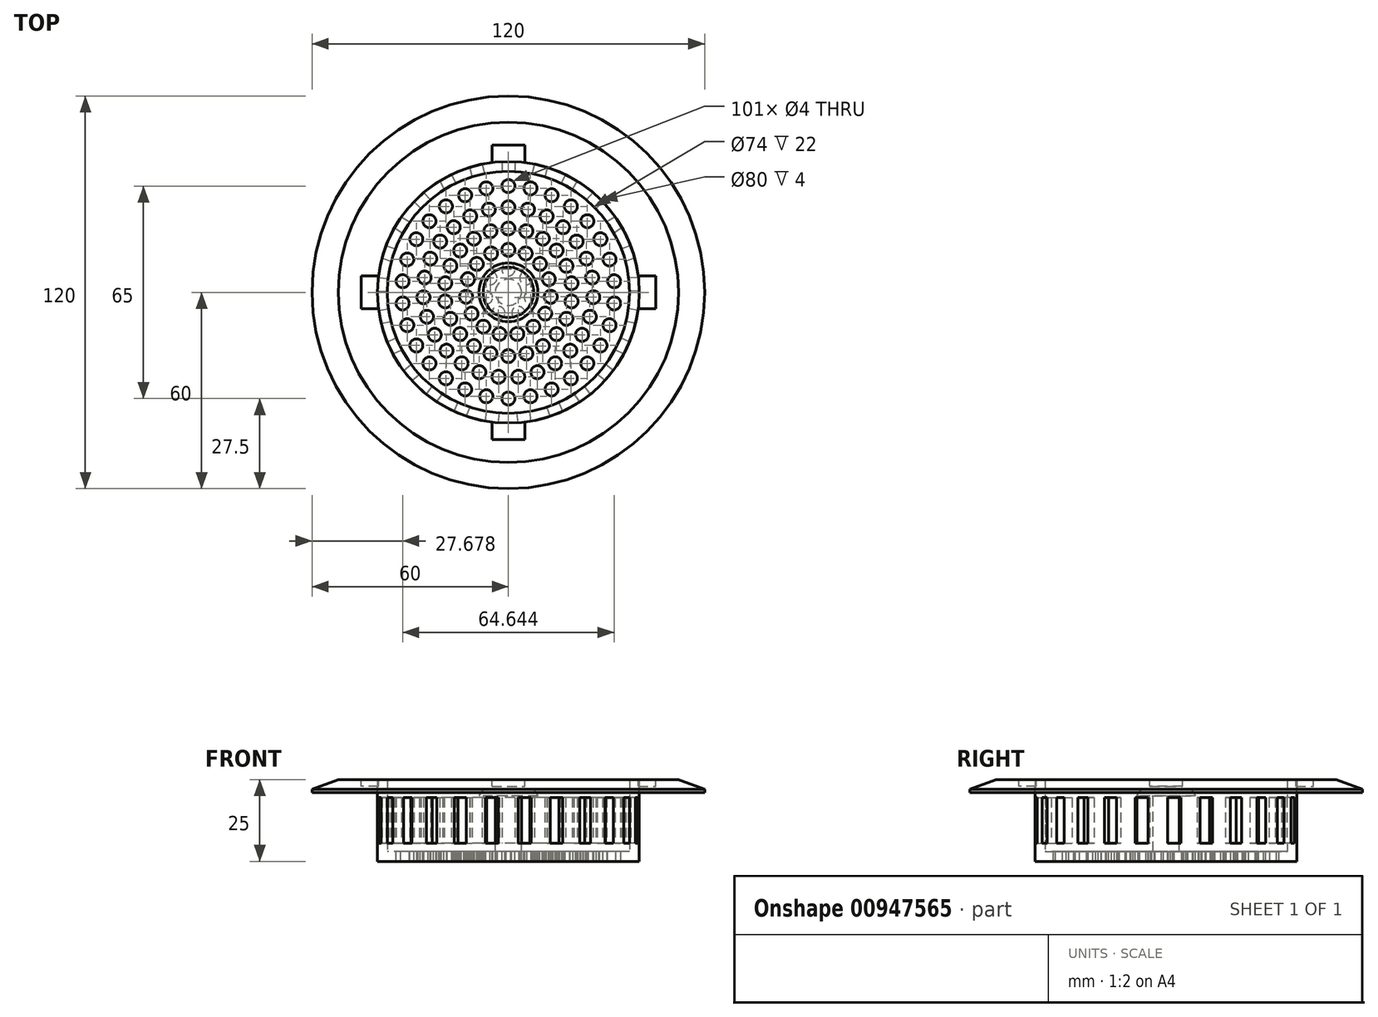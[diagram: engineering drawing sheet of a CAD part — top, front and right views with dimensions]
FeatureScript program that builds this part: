
annotation { "Feature Type Name" : "Feature", "Feature Type Description" : "" }
export const myFeature = defineFeature(function(context is Context, id is Id, definition is map)
    precondition{}
    {
        {
            var Q0;
            Q0=qCreatedBy(makeId("Top.planeOp"),FACE);
            var sketch = newSketch(context, id + "F0", { "sketchPlane" : qUnion([Q0])});
            skCircle(sketch, "E0", {"center": v(0, 0) * mm, "radius": 40 * mm});
            skSolve(sketch);
        }
        {
            var Q0;
            Q0 = qSketchRegion(id + "F0", true);
            extrude(context, id + "F1", {"entities" : qUnion([Q0]), "depth" : 25 * mm, "offsetDistance" : 25 * mm});
        }
        {
            var Q0;
            Q0=makeQuery(id+"F1.opExtrude","CAP_FACE",FACE,{"disambiguationData":[OSD([sQuery(id+"F0.wireOp",EDGE,"E0")])],"isStart":false});
            shell(context, id + "F2", {"entities" : qUnion([Q0]), "thickness" : 3 * mm});
        }
        {
            var Q0;
            Q0=makeQuery(id+"F1.opExtrude","CAP_FACE",FACE,{"disambiguationData":[OSD([sQuery(id+"F0.wireOp",EDGE,"E0")])],"isStart":false});
            var sketch = newSketch(context, id + "F3", { "sketchPlane" : qUnion([Q0])});
            skLineSegment(sketch, "E1", {"start": v(-5, 39.69) * mm, "end": v(-5, 45) * mm});
            skLineSegment(sketch, "E2", {"start": v(-5, 45) * mm, "end": v(0, 45) * mm});
            skLineSegment(sketch, "E3.MirrorCS", {"start": v(5, 45) * mm, "end": v(0, 45) * mm});
            skLineSegment(sketch, "E4.MirrorCS", {"start": v(5, 39.69) * mm, "end": v(5, 45) * mm});
            skLineSegment(sketch, "E5.1.0", {"start": v(-39.69, -5) * mm, "end": v(-45, -5) * mm});
            skLineSegment(sketch, "E5.1.1", {"start": v(-45, -5) * mm, "end": v(-45, 0) * mm});
            skLineSegment(sketch, "E5.1.2", {"start": v(-45, 5) * mm, "end": v(-45, 0) * mm});
            skLineSegment(sketch, "E5.1.3", {"start": v(-39.69, 5) * mm, "end": v(-45, 5) * mm});
            skLineSegment(sketch, "E5.2.0", {"start": v(5, -39.69) * mm, "end": v(5, -45) * mm});
            skLineSegment(sketch, "E5.2.1", {"start": v(5, -45) * mm, "end": v(0, -45) * mm});
            skLineSegment(sketch, "E5.2.2", {"start": v(-5, -45) * mm, "end": v(0, -45) * mm});
            skLineSegment(sketch, "E5.2.3", {"start": v(-5, -39.69) * mm, "end": v(-5, -45) * mm});
            skLineSegment(sketch, "E5.3.0", {"start": v(39.69, 5) * mm, "end": v(45, 5) * mm});
            skLineSegment(sketch, "E5.3.1", {"start": v(45, 5) * mm, "end": v(45, 0) * mm});
            skLineSegment(sketch, "E5.3.2", {"start": v(45, -5) * mm, "end": v(45, 0) * mm});
            skLineSegment(sketch, "E5.3.3", {"start": v(39.69, -5) * mm, "end": v(45, -5) * mm});
            skPoint(sketch, "E5.center", {"position": v(0, 0) * mm});
            skSolve(sketch);
        }
        {
            var Q0;
            {var subQ1=sQuery(id+"F3.wireOp",EDGE,"E5.1.0");Q0=makeQuery(id+"F3.imprint","IMPRINT",FACE,{"disambiguationData":[TD([[makeQuery(id+"F3.imprint","IMPRINT",EDGE,{"derivedFrom":subQ1}),-1.0]])]});}
            var Q1;
            {var subQ1=sQuery(id+"F3.wireOp",EDGE,"E1");Q1=makeQuery(id+"F3.imprint","IMPRINT",FACE,{"disambiguationData":[TD([[makeQuery(id+"F3.imprint","IMPRINT",EDGE,{"derivedFrom":subQ1}),-1.0]])]});}
            var Q2;
            {var subQ1=sQuery(id+"F3.wireOp",EDGE,"E5.3.0");Q2=makeQuery(id+"F3.imprint","IMPRINT",FACE,{"disambiguationData":[TD([[makeQuery(id+"F3.imprint","IMPRINT",EDGE,{"derivedFrom":subQ1}),-1.0]])]});}
            var Q3;
            {var subQ1=sQuery(id+"F3.wireOp",EDGE,"E5.2.0");Q3=makeQuery(id+"F3.imprint","IMPRINT",FACE,{"disambiguationData":[TD([[makeQuery(id+"F3.imprint","IMPRINT",EDGE,{"derivedFrom":subQ1}),-1.0]])]});}
            extrude(context, id + "F4", {"entities" : qUnion([Q0, Q1, Q2, Q3]), "operationType" : NewBodyOperationType.ADD, "oppositeDirection" : true, "depth" : 2 * mm, "offsetDistance" : 25 * mm});
        }
        {
            var Q0;
            {var subQ0=sQuery(id+"F0.wireOp",EDGE,"E0");Q0=makeQuery(id+"F4.boolean.opBoolean","MERGE",FACE,{"derivedFrom":[makeQuery(id+"F1.opExtrude","CAP_FACE",FACE,{"disambiguationData":[OSD([subQ0])],"isStart":false}),makeQuery(id+"F4.opExtrude","CAP_FACE",FACE,{"disambiguationData":[OSD([subQ0,sQuery(id+"F3.wireOp",EDGE,"E1"),sQuery(id+"F3.wireOp",EDGE,"E2"),sQuery(id+"F3.wireOp",EDGE,"E3.MirrorCS"),sQuery(id+"F3.wireOp",EDGE,"E4.MirrorCS")])],"isStart":true}),makeQuery(id+"F4.opExtrude","CAP_FACE",FACE,{"disambiguationData":[OSD([subQ0,sQuery(id+"F3.wireOp",EDGE,"E5.1.0"),sQuery(id+"F3.wireOp",EDGE,"E5.1.1"),sQuery(id+"F3.wireOp",EDGE,"E5.1.2"),sQuery(id+"F3.wireOp",EDGE,"E5.1.3")])],"isStart":true}),makeQuery(id+"F4.opExtrude","CAP_FACE",FACE,{"disambiguationData":[OSD([subQ0,sQuery(id+"F3.wireOp",EDGE,"E5.2.0"),sQuery(id+"F3.wireOp",EDGE,"E5.2.1"),sQuery(id+"F3.wireOp",EDGE,"E5.2.2"),sQuery(id+"F3.wireOp",EDGE,"E5.2.3")])],"isStart":true}),makeQuery(id+"F4.opExtrude","CAP_FACE",FACE,{"disambiguationData":[OSD([subQ0,sQuery(id+"F3.wireOp",EDGE,"E5.3.0"),sQuery(id+"F3.wireOp",EDGE,"E5.3.1"),sQuery(id+"F3.wireOp",EDGE,"E5.3.2"),sQuery(id+"F3.wireOp",EDGE,"E5.3.3")])],"isStart":true})]});}
            var sketch = newSketch(context, id + "F5", { "sketchPlane" : qUnion([Q0])});
            skCircle(sketch, "E6", {"center": v(0, 0) * mm, "radius": 40 * mm});
            skCircle(sketch, "E7.0", {"center": v(0, 0) * mm, "radius": 60 * mm});
            skSolve(sketch);
        }
        {
            var Q0;
            Q0 = qSketchRegion(id + "F5", true);
            extrude(context, id + "F6", {"entities" : qUnion([Q0]), "oppositeDirection" : true, "depth" : 4 * mm, "offsetDistance" : 25 * mm});
        }
        {
            var Q0;
            {var subQ1=sQuery(id+"F3.wireOp",EDGE,"E1");Q0=makeQuery(id+"F3.imprint","IMPRINT",FACE,{"disambiguationData":[TD([[makeQuery(id+"F3.imprint","IMPRINT",EDGE,{"derivedFrom":subQ1}),-1.0]])]});}
            var Q1;
            {var subQ1=sQuery(id+"F3.wireOp",EDGE,"E5.3.0");Q1=makeQuery(id+"F3.imprint","IMPRINT",FACE,{"disambiguationData":[TD([[makeQuery(id+"F3.imprint","IMPRINT",EDGE,{"derivedFrom":subQ1}),-1.0]])]});}
            var Q2;
            {var subQ1=sQuery(id+"F3.wireOp",EDGE,"E5.2.0");Q2=makeQuery(id+"F3.imprint","IMPRINT",FACE,{"disambiguationData":[TD([[makeQuery(id+"F3.imprint","IMPRINT",EDGE,{"derivedFrom":subQ1}),-1.0]])]});}
            var Q3;
            {var subQ1=sQuery(id+"F3.wireOp",EDGE,"E5.1.0");Q3=makeQuery(id+"F3.imprint","IMPRINT",FACE,{"disambiguationData":[TD([[makeQuery(id+"F3.imprint","IMPRINT",EDGE,{"derivedFrom":subQ1}),-1.0]])]});}
            extrude(context, id + "F7", {"entities" : qUnion([Q0, Q1, Q2, Q3]), "operationType" : NewBodyOperationType.REMOVE, "oppositeDirection" : true, "depth" : 2 * mm, "offsetDistance" : 25 * mm});
        }
        {
            var Q0;
            {var subQ0=sQuery(id+"F0.wireOp",EDGE,"E0");Q0=makeQuery(id+"F2.opShell","OFFSET_FACE",FACE,{"disambiguationData":[OSD([subQ0]),TDD([makeQuery(id+"F1.opExtrude","CAP_FACE",FACE,{"disambiguationData":[OSD([subQ0])],"isStart":true})])]});}
            var sketch = newSketch(context, id + "F8", { "sketchPlane" : qUnion([Q0])});
            skLineSegment(sketch, "E8", {"start": v(0, 82.02) * mm, "end": v(0, -74.82) * mm, "construction": true});
            skLineSegment(sketch, "E9", {"start": v(79.98, 0) * mm, "end": v(-98.2, 0) * mm, "construction": true});
            skCircle(sketch, "E10", {"center": v(0, 32.5) * mm, "radius": 2 * mm});
            skCircle(sketch, "E11", {"center": v(0, 26) * mm, "radius": 2 * mm});
            skCircle(sketch, "E12", {"center": v(0, 19.5) * mm, "radius": 2 * mm});
            skCircle(sketch, "E13", {"center": v(0, 13) * mm, "radius": 2 * mm});
            skCircle(sketch, "E14", {"center": v(0, 7) * mm, "radius": 2 * mm});
            skCircle(sketch, "E15.1.0", {"center": v(-6.76, 31.79) * mm, "radius": 2 * mm});
            skCircle(sketch, "E15.2.0", {"center": v(-13.22, 29.7) * mm, "radius": 2 * mm});
            skCircle(sketch, "E15.3.0", {"center": v(-19.1, 26.3) * mm, "radius": 2 * mm});
            skCircle(sketch, "E15.4.0", {"center": v(-24.15, 21.75) * mm, "radius": 2 * mm});
            skCircle(sketch, "E15.5.0", {"center": v(-28.15, 16.25) * mm, "radius": 2 * mm});
            skCircle(sketch, "E15.6.0", {"center": v(-30.9, 10.04) * mm, "radius": 2 * mm});
            skCircle(sketch, "E15.7.0", {"center": v(-32.32, 3.4) * mm, "radius": 2 * mm});
            skCircle(sketch, "E15.8.0", {"center": v(-32.32, -3.4) * mm, "radius": 2 * mm});
            skCircle(sketch, "E15.9.0", {"center": v(-30.9, -10.04) * mm, "radius": 2 * mm});
            skCircle(sketch, "E15.10.0", {"center": v(-28.15, -16.25) * mm, "radius": 2 * mm});
            skCircle(sketch, "E15.11.0", {"center": v(-24.15, -21.75) * mm, "radius": 2 * mm});
            skCircle(sketch, "E15.12.0", {"center": v(-19.1, -26.3) * mm, "radius": 2 * mm});
            skCircle(sketch, "E15.13.0", {"center": v(-13.22, -29.7) * mm, "radius": 2 * mm});
            skCircle(sketch, "E15.14.0", {"center": v(-6.76, -31.79) * mm, "radius": 2 * mm});
            skCircle(sketch, "E15.15.0", {"center": v(0, -32.5) * mm, "radius": 2 * mm});
            skCircle(sketch, "E15.16.0", {"center": v(6.76, -31.79) * mm, "radius": 2 * mm});
            skCircle(sketch, "E15.17.0", {"center": v(13.22, -29.7) * mm, "radius": 2 * mm});
            skCircle(sketch, "E15.18.0", {"center": v(19.1, -26.3) * mm, "radius": 2 * mm});
            skCircle(sketch, "E15.19.0", {"center": v(24.15, -21.75) * mm, "radius": 2 * mm});
            skCircle(sketch, "E15.20.0", {"center": v(28.15, -16.25) * mm, "radius": 2 * mm});
            skCircle(sketch, "E15.21.0", {"center": v(30.9, -10.04) * mm, "radius": 2 * mm});
            skCircle(sketch, "E15.22.0", {"center": v(32.32, -3.4) * mm, "radius": 2 * mm});
            skCircle(sketch, "E15.23.0", {"center": v(32.32, 3.4) * mm, "radius": 2 * mm});
            skCircle(sketch, "E15.24.0", {"center": v(30.9, 10.04) * mm, "radius": 2 * mm});
            skCircle(sketch, "E15.25.0", {"center": v(28.15, 16.25) * mm, "radius": 2 * mm});
            skCircle(sketch, "E15.26.0", {"center": v(24.15, 21.75) * mm, "radius": 2 * mm});
            skCircle(sketch, "E15.27.0", {"center": v(19.1, 26.3) * mm, "radius": 2 * mm});
            skCircle(sketch, "E15.28.0", {"center": v(13.22, 29.7) * mm, "radius": 2 * mm});
            skCircle(sketch, "E15.29.0", {"center": v(6.76, 31.79) * mm, "radius": 2 * mm});
            skPoint(sketch, "E15.center", {"position": v(0, 0) * mm});
            skCircle(sketch, "E16.1.0", {"center": v(-6, 25.3) * mm, "radius": 2 * mm});
            skCircle(sketch, "E16.2.0", {"center": v(-11.67, 23.23) * mm, "radius": 2 * mm});
            skCircle(sketch, "E16.3.0", {"center": v(-16.71, 19.92) * mm, "radius": 2 * mm});
            skCircle(sketch, "E16.4.0", {"center": v(-20.86, 15.53) * mm, "radius": 2 * mm});
            skCircle(sketch, "E16.5.0", {"center": v(-23.87, 10.3) * mm, "radius": 2 * mm});
            skCircle(sketch, "E16.6.0", {"center": v(-25.6, 4.51) * mm, "radius": 2 * mm});
            skCircle(sketch, "E16.7.0", {"center": v(-25.96, -1.51) * mm, "radius": 2 * mm});
            skCircle(sketch, "E16.8.0", {"center": v(-24.9, -7.46) * mm, "radius": 2 * mm});
            skCircle(sketch, "E16.9.0", {"center": v(-22.52, -13) * mm, "radius": 2 * mm});
            skCircle(sketch, "E16.10.0", {"center": v(-18.91, -17.84) * mm, "radius": 2 * mm});
            skCircle(sketch, "E16.11.0", {"center": v(-14.29, -21.72) * mm, "radius": 2 * mm});
            skCircle(sketch, "E16.12.0", {"center": v(-8.9, -24.43) * mm, "radius": 2 * mm});
            skCircle(sketch, "E16.13.0", {"center": v(-3.02, -25.82) * mm, "radius": 2 * mm});
            skCircle(sketch, "E16.14.0", {"center": v(3.02, -25.82) * mm, "radius": 2 * mm});
            skCircle(sketch, "E16.15.0", {"center": v(8.9, -24.43) * mm, "radius": 2 * mm});
            skCircle(sketch, "E16.16.0", {"center": v(14.29, -21.72) * mm, "radius": 2 * mm});
            skCircle(sketch, "E16.17.0", {"center": v(18.91, -17.84) * mm, "radius": 2 * mm});
            skCircle(sketch, "E16.18.0", {"center": v(22.52, -13) * mm, "radius": 2 * mm});
            skCircle(sketch, "E16.19.0", {"center": v(24.9, -7.46) * mm, "radius": 2 * mm});
            skCircle(sketch, "E16.20.0", {"center": v(25.96, -1.51) * mm, "radius": 2 * mm});
            skCircle(sketch, "E16.21.0", {"center": v(25.6, 4.51) * mm, "radius": 2 * mm});
            skCircle(sketch, "E16.22.0", {"center": v(23.87, 10.3) * mm, "radius": 2 * mm});
            skCircle(sketch, "E16.23.0", {"center": v(20.86, 15.53) * mm, "radius": 2 * mm});
            skCircle(sketch, "E16.24.0", {"center": v(16.71, 19.92) * mm, "radius": 2 * mm});
            skCircle(sketch, "E16.25.0", {"center": v(11.67, 23.23) * mm, "radius": 2 * mm});
            skCircle(sketch, "E16.26.0", {"center": v(6, 25.3) * mm, "radius": 2 * mm});
            skCircle(sketch, "E17.1.0", {"center": v(-5.5, 18.71) * mm, "radius": 2 * mm});
            skCircle(sketch, "E17.2.0", {"center": v(-10.54, 16.4) * mm, "radius": 2 * mm});
            skCircle(sketch, "E17.3.0", {"center": v(-14.74, 12.77) * mm, "radius": 2 * mm});
            skCircle(sketch, "E17.4.0", {"center": v(-17.74, 8.1) * mm, "radius": 2 * mm});
            skCircle(sketch, "E17.5.0", {"center": v(-19.3, 2.78) * mm, "radius": 2 * mm});
            skCircle(sketch, "E17.6.0", {"center": v(-19.3, -2.78) * mm, "radius": 2 * mm});
            skCircle(sketch, "E17.7.0", {"center": v(-17.74, -8.1) * mm, "radius": 2 * mm});
            skCircle(sketch, "E17.8.0", {"center": v(-14.74, -12.77) * mm, "radius": 2 * mm});
            skCircle(sketch, "E17.9.0", {"center": v(-10.54, -16.4) * mm, "radius": 2 * mm});
            skCircle(sketch, "E17.10.0", {"center": v(-5.5, -18.71) * mm, "radius": 2 * mm});
            skCircle(sketch, "E17.11.0", {"center": v(0, -19.5) * mm, "radius": 2 * mm});
            skCircle(sketch, "E17.12.0", {"center": v(5.5, -18.71) * mm, "radius": 2 * mm});
            skCircle(sketch, "E17.13.0", {"center": v(10.54, -16.4) * mm, "radius": 2 * mm});
            skCircle(sketch, "E17.14.0", {"center": v(14.74, -12.77) * mm, "radius": 2 * mm});
            skCircle(sketch, "E17.15.0", {"center": v(17.74, -8.1) * mm, "radius": 2 * mm});
            skCircle(sketch, "E17.16.0", {"center": v(19.3, -2.78) * mm, "radius": 2 * mm});
            skCircle(sketch, "E17.17.0", {"center": v(19.3, 2.78) * mm, "radius": 2 * mm});
            skCircle(sketch, "E17.18.0", {"center": v(17.74, 8.1) * mm, "radius": 2 * mm});
            skCircle(sketch, "E17.19.0", {"center": v(14.74, 12.77) * mm, "radius": 2 * mm});
            skCircle(sketch, "E17.20.0", {"center": v(10.54, 16.4) * mm, "radius": 2 * mm});
            skCircle(sketch, "E17.21.0", {"center": v(5.5, 18.71) * mm, "radius": 2 * mm});
            skCircle(sketch, "E18.1.0", {"center": v(-5.29, 11.88) * mm, "radius": 2 * mm});
            skCircle(sketch, "E18.2.0", {"center": v(-9.66, 8.7) * mm, "radius": 2 * mm});
            skCircle(sketch, "E18.3.0", {"center": v(-12.36, 4.02) * mm, "radius": 2 * mm});
            skCircle(sketch, "E18.4.0", {"center": v(-12.93, -1.36) * mm, "radius": 2 * mm});
            skCircle(sketch, "E18.5.0", {"center": v(-11.26, -6.5) * mm, "radius": 2 * mm});
            skCircle(sketch, "E18.6.0", {"center": v(-7.64, -10.52) * mm, "radius": 2 * mm});
            skCircle(sketch, "E18.7.0", {"center": v(-2.7, -12.72) * mm, "radius": 2 * mm});
            skCircle(sketch, "E18.8.0", {"center": v(2.7, -12.72) * mm, "radius": 2 * mm});
            skCircle(sketch, "E18.9.0", {"center": v(7.64, -10.52) * mm, "radius": 2 * mm});
            skCircle(sketch, "E18.10.0", {"center": v(11.26, -6.5) * mm, "radius": 2 * mm});
            skCircle(sketch, "E18.11.0", {"center": v(12.93, -1.36) * mm, "radius": 2 * mm});
            skCircle(sketch, "E18.12.0", {"center": v(12.36, 4.02) * mm, "radius": 2 * mm});
            skCircle(sketch, "E18.13.0", {"center": v(9.66, 8.7) * mm, "radius": 2 * mm});
            skCircle(sketch, "E18.14.0", {"center": v(5.29, 11.88) * mm, "radius": 2 * mm});
            skCircle(sketch, "E19.1.0", {"center": v(-5.47, 4.36) * mm, "radius": 2 * mm});
            skCircle(sketch, "E19.2.0", {"center": v(-6.82, -1.56) * mm, "radius": 2 * mm});
            skCircle(sketch, "E19.3.0", {"center": v(-3.04, -6.3) * mm, "radius": 2 * mm});
            skCircle(sketch, "E19.4.0", {"center": v(3.04, -6.3) * mm, "radius": 2 * mm});
            skCircle(sketch, "E19.5.0", {"center": v(6.82, -1.56) * mm, "radius": 2 * mm});
            skCircle(sketch, "E19.6.0", {"center": v(5.47, 4.36) * mm, "radius": 2 * mm});
            skSolve(sketch);
        }
        {
            var Q0;
            Q0=makeQuery(id+"F8.imprint","IMPRINT",FACE,{"disambiguationData":[TD([[makeQuery(id+"F8.imprint","IMPRINT",EDGE,{"derivedFrom":sQuery(id+"F8.wireOp",EDGE,"E15.21.0")}),1.0]])]});
            var Q1;
            Q1=makeQuery(id+"F8.imprint","IMPRINT",FACE,{"disambiguationData":[TD([[makeQuery(id+"F8.imprint","IMPRINT",EDGE,{"derivedFrom":sQuery(id+"F8.wireOp",EDGE,"E15.3.0")}),1.0]])]});
            var Q2;
            Q2=makeQuery(id+"F8.imprint","IMPRINT",FACE,{"disambiguationData":[TD([[makeQuery(id+"F8.imprint","IMPRINT",EDGE,{"derivedFrom":sQuery(id+"F8.wireOp",EDGE,"E16.11.0")}),1.0]])]});
            var Q3;
            Q3=makeQuery(id+"F8.imprint","IMPRINT",FACE,{"disambiguationData":[TD([[makeQuery(id+"F8.imprint","IMPRINT",EDGE,{"derivedFrom":sQuery(id+"F8.wireOp",EDGE,"E16.8.0")}),1.0]])]});
            var Q4;
            Q4=makeQuery(id+"F8.imprint","IMPRINT",FACE,{"disambiguationData":[TD([[makeQuery(id+"F8.imprint","IMPRINT",EDGE,{"derivedFrom":sQuery(id+"F8.wireOp",EDGE,"E15.22.0")}),1.0]])]});
            var Q5;
            Q5=makeQuery(id+"F8.imprint","IMPRINT",FACE,{"disambiguationData":[TD([[makeQuery(id+"F8.imprint","IMPRINT",EDGE,{"derivedFrom":sQuery(id+"F8.wireOp",EDGE,"E19.1.0")}),1.0]])]});
            var Q6;
            Q6=makeQuery(id+"F8.imprint","IMPRINT",FACE,{"disambiguationData":[TD([[makeQuery(id+"F8.imprint","IMPRINT",EDGE,{"derivedFrom":sQuery(id+"F8.wireOp",EDGE,"E14")}),1.0]])]});
            var Q7;
            Q7=makeQuery(id+"F8.imprint","IMPRINT",FACE,{"disambiguationData":[TD([[makeQuery(id+"F8.imprint","IMPRINT",EDGE,{"derivedFrom":sQuery(id+"F8.wireOp",EDGE,"E15.20.0")}),1.0]])]});
            var Q8;
            Q8=makeQuery(id+"F8.imprint","IMPRINT",FACE,{"disambiguationData":[TD([[makeQuery(id+"F8.imprint","IMPRINT",EDGE,{"derivedFrom":sQuery(id+"F8.wireOp",EDGE,"73012136-396f-4f49-aa01-cc9f4acf6e96.2.0")}),1.0]])]});
            var Q9;
            Q9=makeQuery(id+"F8.imprint","IMPRINT",FACE,{"disambiguationData":[TD([[makeQuery(id+"F8.imprint","IMPRINT",EDGE,{"derivedFrom":sQuery(id+"F8.wireOp",EDGE,"E16.1.0")}),1.0]])]});
            var Q10;
            Q10=makeQuery(id+"F8.imprint","IMPRINT",FACE,{"disambiguationData":[TD([[makeQuery(id+"F8.imprint","IMPRINT",EDGE,{"derivedFrom":sQuery(id+"F8.wireOp",EDGE,"E15.23.0")}),1.0]])]});
            var Q11;
            Q11=makeQuery(id+"F8.imprint","IMPRINT",FACE,{"disambiguationData":[TD([[makeQuery(id+"F8.imprint","IMPRINT",EDGE,{"derivedFrom":sQuery(id+"F8.wireOp",EDGE,"E18.7.0")}),1.0]])]});
            var Q12;
            Q12=makeQuery(id+"F8.imprint","IMPRINT",FACE,{"disambiguationData":[TD([[makeQuery(id+"F8.imprint","IMPRINT",EDGE,{"derivedFrom":sQuery(id+"F8.wireOp",EDGE,"E16.24.0")}),1.0]])]});
            var Q13;
            Q13=makeQuery(id+"F8.imprint","IMPRINT",FACE,{"disambiguationData":[TD([[makeQuery(id+"F8.imprint","IMPRINT",EDGE,{"derivedFrom":sQuery(id+"F8.wireOp",EDGE,"E17.20.0")}),1.0]])]});
            var Q14;
            Q14=makeQuery(id+"F8.imprint","IMPRINT",FACE,{"disambiguationData":[TD([[makeQuery(id+"F8.imprint","IMPRINT",EDGE,{"derivedFrom":sQuery(id+"F8.wireOp",EDGE,"E17.19.0")}),1.0]])]});
            var Q15;
            Q15=makeQuery(id+"F8.imprint","IMPRINT",FACE,{"disambiguationData":[TD([[makeQuery(id+"F8.imprint","IMPRINT",EDGE,{"derivedFrom":sQuery(id+"F8.wireOp",EDGE,"E15.24.0")}),1.0]])]});
            var Q16;
            Q16=makeQuery(id+"F8.imprint","IMPRINT",FACE,{"disambiguationData":[TD([[makeQuery(id+"F8.imprint","IMPRINT",EDGE,{"derivedFrom":sQuery(id+"F8.wireOp",EDGE,"E15.14.0")}),1.0]])]});
            var Q17;
            Q17=makeQuery(id+"F8.imprint","IMPRINT",FACE,{"disambiguationData":[TD([[makeQuery(id+"F8.imprint","IMPRINT",EDGE,{"derivedFrom":sQuery(id+"F8.wireOp",EDGE,"E15.2.0")}),1.0]])]});
            var Q18;
            Q18=makeQuery(id+"F8.imprint","IMPRINT",FACE,{"disambiguationData":[TD([[makeQuery(id+"F8.imprint","IMPRINT",EDGE,{"derivedFrom":sQuery(id+"F8.wireOp",EDGE,"E16.2.0")}),1.0]])]});
            var Q19;
            Q19=makeQuery(id+"F8.imprint","IMPRINT",FACE,{"disambiguationData":[TD([[makeQuery(id+"F8.imprint","IMPRINT",EDGE,{"derivedFrom":sQuery(id+"F8.wireOp",EDGE,"E17.16.0")}),1.0]])]});
            var Q20;
            Q20=makeQuery(id+"F8.imprint","IMPRINT",FACE,{"disambiguationData":[TD([[makeQuery(id+"F8.imprint","IMPRINT",EDGE,{"derivedFrom":sQuery(id+"F8.wireOp",EDGE,"E16.25.0")}),1.0]])]});
            var Q21;
            Q21=makeQuery(id+"F8.imprint","IMPRINT",FACE,{"disambiguationData":[TD([[makeQuery(id+"F8.imprint","IMPRINT",EDGE,{"derivedFrom":sQuery(id+"F8.wireOp",EDGE,"E16.22.0")}),1.0]])]});
            var Q22;
            Q22=makeQuery(id+"F8.imprint","IMPRINT",FACE,{"disambiguationData":[TD([[makeQuery(id+"F8.imprint","IMPRINT",EDGE,{"derivedFrom":sQuery(id+"F8.wireOp",EDGE,"E16.5.0")}),1.0]])]});
            var Q23;
            Q23=makeQuery(id+"F8.imprint","IMPRINT",FACE,{"disambiguationData":[TD([[makeQuery(id+"F8.imprint","IMPRINT",EDGE,{"derivedFrom":sQuery(id+"F8.wireOp",EDGE,"E18.3.0")}),1.0]])]});
            var Q24;
            Q24=makeQuery(id+"F8.imprint","IMPRINT",FACE,{"disambiguationData":[TD([[makeQuery(id+"F8.imprint","IMPRINT",EDGE,{"derivedFrom":sQuery(id+"F8.wireOp",EDGE,"E15.6.0")}),1.0]])]});
            var Q25;
            Q25=makeQuery(id+"F8.imprint","IMPRINT",FACE,{"disambiguationData":[TD([[makeQuery(id+"F8.imprint","IMPRINT",EDGE,{"derivedFrom":sQuery(id+"F8.wireOp",EDGE,"73012136-396f-4f49-aa01-cc9f4acf6e96.1.0")}),1.0]])]});
            var Q26;
            Q26=makeQuery(id+"F8.imprint","IMPRINT",FACE,{"disambiguationData":[TD([[makeQuery(id+"F8.imprint","IMPRINT",EDGE,{"derivedFrom":sQuery(id+"F8.wireOp",EDGE,"E17.22.0")}),1.0]])]});
            var Q27;
            Q27=makeQuery(id+"F8.imprint","IMPRINT",FACE,{"disambiguationData":[TD([[makeQuery(id+"F8.imprint","IMPRINT",EDGE,{"derivedFrom":sQuery(id+"F8.wireOp",EDGE,"E18.1.0")}),1.0]])]});
            var Q28;
            Q28=makeQuery(id+"F8.imprint","IMPRINT",FACE,{"disambiguationData":[TD([[makeQuery(id+"F8.imprint","IMPRINT",EDGE,{"derivedFrom":sQuery(id+"F8.wireOp",EDGE,"E18.5.0")}),1.0]])]});
            var Q29;
            Q29=makeQuery(id+"F8.imprint","IMPRINT",FACE,{"disambiguationData":[TD([[makeQuery(id+"F8.imprint","IMPRINT",EDGE,{"derivedFrom":sQuery(id+"F8.wireOp",EDGE,"E16.3.0")}),1.0]])]});
            var Q30;
            Q30=makeQuery(id+"F8.imprint","IMPRINT",FACE,{"disambiguationData":[TD([[makeQuery(id+"F8.imprint","IMPRINT",EDGE,{"derivedFrom":sQuery(id+"F8.wireOp",EDGE,"E15.9.0")}),1.0]])]});
            var Q31;
            Q31=makeQuery(id+"F8.imprint","IMPRINT",FACE,{"disambiguationData":[TD([[makeQuery(id+"F8.imprint","IMPRINT",EDGE,{"derivedFrom":sQuery(id+"F8.wireOp",EDGE,"E15.15.0")}),1.0]])]});
            var Q32;
            Q32=makeQuery(id+"F8.imprint","IMPRINT",FACE,{"disambiguationData":[TD([[makeQuery(id+"F8.imprint","IMPRINT",EDGE,{"derivedFrom":sQuery(id+"F8.wireOp",EDGE,"E16.9.0")}),1.0]])]});
            var Q33;
            Q33=makeQuery(id+"F8.imprint","IMPRINT",FACE,{"disambiguationData":[TD([[makeQuery(id+"F8.imprint","IMPRINT",EDGE,{"derivedFrom":sQuery(id+"F8.wireOp",EDGE,"E15.5.0")}),1.0]])]});
            var Q34;
            Q34=makeQuery(id+"F8.imprint","IMPRINT",FACE,{"disambiguationData":[TD([[makeQuery(id+"F8.imprint","IMPRINT",EDGE,{"derivedFrom":sQuery(id+"F8.wireOp",EDGE,"E17.3.0")}),1.0]])]});
            var Q35;
            Q35=makeQuery(id+"F8.imprint","IMPRINT",FACE,{"disambiguationData":[TD([[makeQuery(id+"F8.imprint","IMPRINT",EDGE,{"derivedFrom":sQuery(id+"F8.wireOp",EDGE,"E12")}),1.0]])]});
            var Q36;
            Q36=makeQuery(id+"F8.imprint","IMPRINT",FACE,{"disambiguationData":[TD([[makeQuery(id+"F8.imprint","IMPRINT",EDGE,{"derivedFrom":sQuery(id+"F8.wireOp",EDGE,"E11")}),1.0]])]});
            var Q37;
            Q37=makeQuery(id+"F8.imprint","IMPRINT",FACE,{"disambiguationData":[TD([[makeQuery(id+"F8.imprint","IMPRINT",EDGE,{"derivedFrom":sQuery(id+"F8.wireOp",EDGE,"E18.9.0")}),1.0]])]});
            var Q38;
            Q38=makeQuery(id+"F8.imprint","IMPRINT",FACE,{"disambiguationData":[TD([[makeQuery(id+"F8.imprint","IMPRINT",EDGE,{"derivedFrom":sQuery(id+"F8.wireOp",EDGE,"E16.12.0")}),1.0]])]});
            var Q39;
            Q39=makeQuery(id+"F8.imprint","IMPRINT",FACE,{"disambiguationData":[TD([[makeQuery(id+"F8.imprint","IMPRINT",EDGE,{"derivedFrom":sQuery(id+"F8.wireOp",EDGE,"E15.7.0")}),1.0]])]});
            var Q40;
            Q40=makeQuery(id+"F8.imprint","IMPRINT",FACE,{"disambiguationData":[TD([[makeQuery(id+"F8.imprint","IMPRINT",EDGE,{"derivedFrom":sQuery(id+"F8.wireOp",EDGE,"E15.12.0")}),1.0]])]});
            var Q41;
            Q41=makeQuery(id+"F8.imprint","IMPRINT",FACE,{"disambiguationData":[TD([[makeQuery(id+"F8.imprint","IMPRINT",EDGE,{"derivedFrom":sQuery(id+"F8.wireOp",EDGE,"E18.12.0")}),1.0]])]});
            var Q42;
            Q42=makeQuery(id+"F8.imprint","IMPRINT",FACE,{"disambiguationData":[TD([[makeQuery(id+"F8.imprint","IMPRINT",EDGE,{"derivedFrom":sQuery(id+"F8.wireOp",EDGE,"E16.13.0")}),1.0]])]});
            var Q43;
            Q43=makeQuery(id+"F8.imprint","IMPRINT",FACE,{"disambiguationData":[TD([[makeQuery(id+"F8.imprint","IMPRINT",EDGE,{"derivedFrom":sQuery(id+"F8.wireOp",EDGE,"E19.4.0")}),1.0]])]});
            var Q44;
            Q44=makeQuery(id+"F8.imprint","IMPRINT",FACE,{"disambiguationData":[TD([[makeQuery(id+"F8.imprint","IMPRINT",EDGE,{"derivedFrom":sQuery(id+"F8.wireOp",EDGE,"E16.16.0")}),1.0]])]});
            var Q45;
            Q45=makeQuery(id+"F8.imprint","IMPRINT",FACE,{"disambiguationData":[TD([[makeQuery(id+"F8.imprint","IMPRINT",EDGE,{"derivedFrom":sQuery(id+"F8.wireOp",EDGE,"E16.4.0")}),1.0]])]});
            var Q46;
            Q46=makeQuery(id+"F8.imprint","IMPRINT",FACE,{"disambiguationData":[TD([[makeQuery(id+"F8.imprint","IMPRINT",EDGE,{"derivedFrom":sQuery(id+"F8.wireOp",EDGE,"E16.7.0")}),1.0]])]});
            var Q47;
            Q47=makeQuery(id+"F8.imprint","IMPRINT",FACE,{"disambiguationData":[TD([[makeQuery(id+"F8.imprint","IMPRINT",EDGE,{"derivedFrom":sQuery(id+"F8.wireOp",EDGE,"E17.6.0")}),1.0]])]});
            var Q48;
            Q48=makeQuery(id+"F8.imprint","IMPRINT",FACE,{"disambiguationData":[TD([[makeQuery(id+"F8.imprint","IMPRINT",EDGE,{"derivedFrom":sQuery(id+"F8.wireOp",EDGE,"E15.19.0")}),1.0]])]});
            var Q49;
            Q49=makeQuery(id+"F8.imprint","IMPRINT",FACE,{"disambiguationData":[TD([[makeQuery(id+"F8.imprint","IMPRINT",EDGE,{"derivedFrom":sQuery(id+"F8.wireOp",EDGE,"E16.15.0")}),1.0]])]});
            var Q50;
            Q50=makeQuery(id+"F8.imprint","IMPRINT",FACE,{"disambiguationData":[TD([[makeQuery(id+"F8.imprint","IMPRINT",EDGE,{"derivedFrom":sQuery(id+"F8.wireOp",EDGE,"E18.10.0")}),1.0]])]});
            var Q51;
            Q51=makeQuery(id+"F8.imprint","IMPRINT",FACE,{"disambiguationData":[TD([[makeQuery(id+"F8.imprint","IMPRINT",EDGE,{"derivedFrom":sQuery(id+"F8.wireOp",EDGE,"E15.1.0")}),1.0]])]});
            var Q52;
            Q52=makeQuery(id+"F8.imprint","IMPRINT",FACE,{"disambiguationData":[TD([[makeQuery(id+"F8.imprint","IMPRINT",EDGE,{"derivedFrom":sQuery(id+"F8.wireOp",EDGE,"E19.11.0")}),1.0]])]});
            var Q53;
            Q53=makeQuery(id+"F8.imprint","IMPRINT",FACE,{"disambiguationData":[TD([[makeQuery(id+"F8.imprint","IMPRINT",EDGE,{"derivedFrom":sQuery(id+"F8.wireOp",EDGE,"73012136-396f-4f49-aa01-cc9f4acf6e96.7.0")}),1.0]])]});
            var Q54;
            Q54=makeQuery(id+"F8.imprint","IMPRINT",FACE,{"disambiguationData":[TD([[makeQuery(id+"F8.imprint","IMPRINT",EDGE,{"derivedFrom":sQuery(id+"F8.wireOp",EDGE,"E15.29.0")}),1.0]])]});
            var Q55;
            Q55=makeQuery(id+"F8.imprint","IMPRINT",FACE,{"disambiguationData":[TD([[makeQuery(id+"F8.imprint","IMPRINT",EDGE,{"derivedFrom":sQuery(id+"F8.wireOp",EDGE,"E18.11.0")}),1.0]])]});
            var Q56;
            Q56=makeQuery(id+"F8.imprint","IMPRINT",FACE,{"disambiguationData":[TD([[makeQuery(id+"F8.imprint","IMPRINT",EDGE,{"derivedFrom":sQuery(id+"F8.wireOp",EDGE,"E17.21.0")}),1.0]])]});
            var Q57;
            Q57=makeQuery(id+"F8.imprint","IMPRINT",FACE,{"disambiguationData":[TD([[makeQuery(id+"F8.imprint","IMPRINT",EDGE,{"derivedFrom":sQuery(id+"F8.wireOp",EDGE,"E16.14.0")}),1.0]])]});
            var Q58;
            Q58=makeQuery(id+"F8.imprint","IMPRINT",FACE,{"disambiguationData":[TD([[makeQuery(id+"F8.imprint","IMPRINT",EDGE,{"derivedFrom":sQuery(id+"F8.wireOp",EDGE,"E16.20.0")}),1.0]])]});
            var Q59;
            Q59=makeQuery(id+"F8.imprint","IMPRINT",FACE,{"disambiguationData":[TD([[makeQuery(id+"F8.imprint","IMPRINT",EDGE,{"derivedFrom":sQuery(id+"F8.wireOp",EDGE,"E19.12.0")}),1.0]])]});
            var Q60;
            Q60=makeQuery(id+"F8.imprint","IMPRINT",FACE,{"disambiguationData":[TD([[makeQuery(id+"F8.imprint","IMPRINT",EDGE,{"derivedFrom":sQuery(id+"F8.wireOp",EDGE,"E16.10.0")}),1.0]])]});
            var Q61;
            Q61=makeQuery(id+"F8.imprint","IMPRINT",FACE,{"disambiguationData":[TD([[makeQuery(id+"F8.imprint","IMPRINT",EDGE,{"derivedFrom":sQuery(id+"F8.wireOp",EDGE,"E15.25.0")}),1.0]])]});
            var Q62;
            Q62=makeQuery(id+"F8.imprint","IMPRINT",FACE,{"disambiguationData":[TD([[makeQuery(id+"F8.imprint","IMPRINT",EDGE,{"derivedFrom":sQuery(id+"F8.wireOp",EDGE,"E18.17.0")}),1.0]])]});
            var Q63;
            Q63=makeQuery(id+"F8.imprint","IMPRINT",FACE,{"disambiguationData":[TD([[makeQuery(id+"F8.imprint","IMPRINT",EDGE,{"derivedFrom":sQuery(id+"F8.wireOp",EDGE,"E18.6.0")}),1.0]])]});
            var Q64;
            Q64=makeQuery(id+"F8.imprint","IMPRINT",FACE,{"disambiguationData":[TD([[makeQuery(id+"F8.imprint","IMPRINT",EDGE,{"derivedFrom":sQuery(id+"F8.wireOp",EDGE,"E19.2.0")}),1.0]])]});
            var Q65;
            Q65=makeQuery(id+"F8.imprint","IMPRINT",FACE,{"disambiguationData":[TD([[makeQuery(id+"F8.imprint","IMPRINT",EDGE,{"derivedFrom":sQuery(id+"F8.wireOp",EDGE,"E18.16.0")}),1.0]])]});
            var Q66;
            Q66=makeQuery(id+"F8.imprint","IMPRINT",FACE,{"disambiguationData":[TD([[makeQuery(id+"F8.imprint","IMPRINT",EDGE,{"derivedFrom":sQuery(id+"F8.wireOp",EDGE,"E16.21.0")}),1.0]])]});
            var Q67;
            Q67=makeQuery(id+"F8.imprint","IMPRINT",FACE,{"disambiguationData":[TD([[makeQuery(id+"F8.imprint","IMPRINT",EDGE,{"derivedFrom":sQuery(id+"F8.wireOp",EDGE,"E10")}),1.0]])]});
            var Q68;
            Q68=makeQuery(id+"F8.imprint","IMPRINT",FACE,{"disambiguationData":[TD([[makeQuery(id+"F8.imprint","IMPRINT",EDGE,{"derivedFrom":sQuery(id+"F8.wireOp",EDGE,"E18.15.0")}),1.0]])]});
            var Q69;
            Q69=makeQuery(id+"F8.imprint","IMPRINT",FACE,{"disambiguationData":[TD([[makeQuery(id+"F8.imprint","IMPRINT",EDGE,{"derivedFrom":sQuery(id+"F8.wireOp",EDGE,"E15.8.0")}),1.0]])]});
            var Q70;
            Q70=makeQuery(id+"F8.imprint","IMPRINT",FACE,{"disambiguationData":[TD([[makeQuery(id+"F8.imprint","IMPRINT",EDGE,{"derivedFrom":sQuery(id+"F8.wireOp",EDGE,"E19.7.0")}),1.0]])]});
            var Q71;
            Q71=makeQuery(id+"F8.imprint","IMPRINT",FACE,{"disambiguationData":[TD([[makeQuery(id+"F8.imprint","IMPRINT",EDGE,{"derivedFrom":sQuery(id+"F8.wireOp",EDGE,"E17.2.0")}),1.0]])]});
            var Q72;
            Q72=makeQuery(id+"F8.imprint","IMPRINT",FACE,{"disambiguationData":[TD([[makeQuery(id+"F8.imprint","IMPRINT",EDGE,{"derivedFrom":sQuery(id+"F8.wireOp",EDGE,"E15.26.0")}),1.0]])]});
            var Q73;
            Q73=makeQuery(id+"F8.imprint","IMPRINT",FACE,{"disambiguationData":[TD([[makeQuery(id+"F8.imprint","IMPRINT",EDGE,{"derivedFrom":sQuery(id+"F8.wireOp",EDGE,"E16.6.0")}),1.0]])]});
            var Q74;
            Q74=makeQuery(id+"F8.imprint","IMPRINT",FACE,{"disambiguationData":[TD([[makeQuery(id+"F8.imprint","IMPRINT",EDGE,{"derivedFrom":sQuery(id+"F8.wireOp",EDGE,"E17.23.0")}),1.0]])]});
            var Q75;
            Q75=makeQuery(id+"F8.imprint","IMPRINT",FACE,{"disambiguationData":[TD([[makeQuery(id+"F8.imprint","IMPRINT",EDGE,{"derivedFrom":sQuery(id+"F8.wireOp",EDGE,"E18.14.0")}),1.0]])]});
            var Q76;
            Q76=makeQuery(id+"F8.imprint","IMPRINT",FACE,{"disambiguationData":[TD([[makeQuery(id+"F8.imprint","IMPRINT",EDGE,{"derivedFrom":sQuery(id+"F8.wireOp",EDGE,"73012136-396f-4f49-aa01-cc9f4acf6e96.5.0")}),1.0]])]});
            var Q77;
            Q77=makeQuery(id+"F8.imprint","IMPRINT",FACE,{"disambiguationData":[TD([[makeQuery(id+"F8.imprint","IMPRINT",EDGE,{"derivedFrom":sQuery(id+"F8.wireOp",EDGE,"73012136-396f-4f49-aa01-cc9f4acf6e96.6.0")}),1.0]])]});
            var Q78;
            Q78=makeQuery(id+"F8.imprint","IMPRINT",FACE,{"disambiguationData":[TD([[makeQuery(id+"F8.imprint","IMPRINT",EDGE,{"derivedFrom":sQuery(id+"F8.wireOp",EDGE,"E15.28.0")}),1.0]])]});
            var Q79;
            Q79=makeQuery(id+"F8.imprint","IMPRINT",FACE,{"disambiguationData":[TD([[makeQuery(id+"F8.imprint","IMPRINT",EDGE,{"derivedFrom":sQuery(id+"F8.wireOp",EDGE,"E15.27.0")}),1.0]])]});
            var Q80;
            Q80=makeQuery(id+"F8.imprint","IMPRINT",FACE,{"disambiguationData":[TD([[makeQuery(id+"F8.imprint","IMPRINT",EDGE,{"derivedFrom":sQuery(id+"F8.wireOp",EDGE,"E18.2.0")}),1.0]])]});
            var Q81;
            Q81=makeQuery(id+"F8.imprint","IMPRINT",FACE,{"disambiguationData":[TD([[makeQuery(id+"F8.imprint","IMPRINT",EDGE,{"derivedFrom":sQuery(id+"F8.wireOp",EDGE,"73012136-396f-4f49-aa01-cc9f4acf6e96.3.0")}),1.0]])]});
            var Q82;
            Q82=makeQuery(id+"F8.imprint","IMPRINT",FACE,{"disambiguationData":[TD([[makeQuery(id+"F8.imprint","IMPRINT",EDGE,{"derivedFrom":sQuery(id+"F8.wireOp",EDGE,"E17.5.0")}),1.0]])]});
            var Q83;
            Q83=makeQuery(id+"F8.imprint","IMPRINT",FACE,{"disambiguationData":[TD([[makeQuery(id+"F8.imprint","IMPRINT",EDGE,{"derivedFrom":sQuery(id+"F8.wireOp",EDGE,"E17.9.0")}),1.0]])]});
            var Q84;
            Q84=makeQuery(id+"F8.imprint","IMPRINT",FACE,{"disambiguationData":[TD([[makeQuery(id+"F8.imprint","IMPRINT",EDGE,{"derivedFrom":sQuery(id+"F8.wireOp",EDGE,"E19.10.0")}),1.0]])]});
            var Q85;
            Q85=makeQuery(id+"F8.imprint","IMPRINT",FACE,{"disambiguationData":[TD([[makeQuery(id+"F8.imprint","IMPRINT",EDGE,{"derivedFrom":sQuery(id+"F8.wireOp",EDGE,"E15.11.0")}),1.0]])]});
            var Q86;
            Q86=makeQuery(id+"F8.imprint","IMPRINT",FACE,{"disambiguationData":[TD([[makeQuery(id+"F8.imprint","IMPRINT",EDGE,{"derivedFrom":sQuery(id+"F8.wireOp",EDGE,"E19.6.0")}),1.0]])]});
            var Q87;
            Q87=makeQuery(id+"F8.imprint","IMPRINT",FACE,{"disambiguationData":[TD([[makeQuery(id+"F8.imprint","IMPRINT",EDGE,{"derivedFrom":sQuery(id+"F8.wireOp",EDGE,"E18.13.0")}),1.0]])]});
            var Q88;
            Q88=makeQuery(id+"F8.imprint","IMPRINT",FACE,{"disambiguationData":[TD([[makeQuery(id+"F8.imprint","IMPRINT",EDGE,{"derivedFrom":sQuery(id+"F8.wireOp",EDGE,"E13")}),1.0]])]});
            var Q89;
            Q89=makeQuery(id+"F8.imprint","IMPRINT",FACE,{"disambiguationData":[TD([[makeQuery(id+"F8.imprint","IMPRINT",EDGE,{"derivedFrom":sQuery(id+"F8.wireOp",EDGE,"bzHftK0l-4Ejx-rRCJ-tJHV-KyST4kjTnBoR")}),1.0]])]});
            var Q90;
            Q90=makeQuery(id+"F8.imprint","IMPRINT",FACE,{"disambiguationData":[TD([[makeQuery(id+"F8.imprint","IMPRINT",EDGE,{"derivedFrom":sQuery(id+"F8.wireOp",EDGE,"E15.18.0")}),1.0]])]});
            var Q91;
            Q91=makeQuery(id+"F8.imprint","IMPRINT",FACE,{"disambiguationData":[TD([[makeQuery(id+"F8.imprint","IMPRINT",EDGE,{"derivedFrom":sQuery(id+"F8.wireOp",EDGE,"E15.17.0")}),1.0]])]});
            var Q92;
            Q92=makeQuery(id+"F8.imprint","IMPRINT",FACE,{"disambiguationData":[TD([[makeQuery(id+"F8.imprint","IMPRINT",EDGE,{"derivedFrom":sQuery(id+"F8.wireOp",EDGE,"E15.16.0")}),1.0]])]});
            var Q93;
            Q93=makeQuery(id+"F8.imprint","IMPRINT",FACE,{"disambiguationData":[TD([[makeQuery(id+"F8.imprint","IMPRINT",EDGE,{"derivedFrom":sQuery(id+"F8.wireOp",EDGE,"73012136-396f-4f49-aa01-cc9f4acf6e96.4.0")}),1.0]])]});
            var Q94;
            Q94=makeQuery(id+"F8.imprint","IMPRINT",FACE,{"disambiguationData":[TD([[makeQuery(id+"F8.imprint","IMPRINT",EDGE,{"derivedFrom":sQuery(id+"F8.wireOp",EDGE,"E16.18.0")}),1.0]])]});
            var Q95;
            Q95=makeQuery(id+"F8.imprint","IMPRINT",FACE,{"disambiguationData":[TD([[makeQuery(id+"F8.imprint","IMPRINT",EDGE,{"derivedFrom":sQuery(id+"F8.wireOp",EDGE,"E16.19.0")}),1.0]])]});
            var Q96;
            Q96=makeQuery(id+"F8.imprint","IMPRINT",FACE,{"disambiguationData":[TD([[makeQuery(id+"F8.imprint","IMPRINT",EDGE,{"derivedFrom":sQuery(id+"F8.wireOp",EDGE,"E16.17.0")}),1.0]])]});
            var Q97;
            Q97=makeQuery(id+"F8.imprint","IMPRINT",FACE,{"disambiguationData":[TD([[makeQuery(id+"F8.imprint","IMPRINT",EDGE,{"derivedFrom":sQuery(id+"F8.wireOp",EDGE,"E17.7.0")}),1.0]])]});
            var Q98;
            Q98=makeQuery(id+"F8.imprint","IMPRINT",FACE,{"disambiguationData":[TD([[makeQuery(id+"F8.imprint","IMPRINT",EDGE,{"derivedFrom":sQuery(id+"F8.wireOp",EDGE,"E17.4.0")}),1.0]])]});
            var Q99;
            Q99=makeQuery(id+"F8.imprint","IMPRINT",FACE,{"disambiguationData":[TD([[makeQuery(id+"F8.imprint","IMPRINT",EDGE,{"derivedFrom":sQuery(id+"F8.wireOp",EDGE,"E17.8.0")}),1.0]])]});
            var Q100;
            Q100=makeQuery(id+"F8.imprint","IMPRINT",FACE,{"disambiguationData":[TD([[makeQuery(id+"F8.imprint","IMPRINT",EDGE,{"derivedFrom":sQuery(id+"F8.wireOp",EDGE,"E17.13.0")}),1.0]])]});
            var Q101;
            Q101=makeQuery(id+"F8.imprint","IMPRINT",FACE,{"disambiguationData":[TD([[makeQuery(id+"F8.imprint","IMPRINT",EDGE,{"derivedFrom":sQuery(id+"F8.wireOp",EDGE,"E17.14.0")}),1.0]])]});
            var Q102;
            Q102=makeQuery(id+"F8.imprint","IMPRINT",FACE,{"disambiguationData":[TD([[makeQuery(id+"F8.imprint","IMPRINT",EDGE,{"derivedFrom":sQuery(id+"F8.wireOp",EDGE,"E17.18.0")}),1.0]])]});
            var Q103;
            Q103=makeQuery(id+"F8.imprint","IMPRINT",FACE,{"disambiguationData":[TD([[makeQuery(id+"F8.imprint","IMPRINT",EDGE,{"derivedFrom":sQuery(id+"F8.wireOp",EDGE,"E16.23.0")}),1.0]])]});
            var Q104;
            Q104=makeQuery(id+"F8.imprint","IMPRINT",FACE,{"disambiguationData":[TD([[makeQuery(id+"F8.imprint","IMPRINT",EDGE,{"derivedFrom":sQuery(id+"F8.wireOp",EDGE,"E16.26.0")}),1.0]])]});
            var Q105;
            Q105=makeQuery(id+"F8.imprint","IMPRINT",FACE,{"disambiguationData":[TD([[makeQuery(id+"F8.imprint","IMPRINT",EDGE,{"derivedFrom":sQuery(id+"F8.wireOp",EDGE,"E16.27.0")}),1.0]])]});
            var Q106;
            Q106=makeQuery(id+"F8.imprint","IMPRINT",FACE,{"disambiguationData":[TD([[makeQuery(id+"F8.imprint","IMPRINT",EDGE,{"derivedFrom":sQuery(id+"F8.wireOp",EDGE,"E17.1.0")}),1.0]])]});
            var Q107;
            Q107=makeQuery(id+"F8.imprint","IMPRINT",FACE,{"disambiguationData":[TD([[makeQuery(id+"F8.imprint","IMPRINT",EDGE,{"derivedFrom":sQuery(id+"F8.wireOp",EDGE,"E15.10.0")}),1.0]])]});
            var Q108;
            Q108=makeQuery(id+"F8.imprint","IMPRINT",FACE,{"disambiguationData":[TD([[makeQuery(id+"F8.imprint","IMPRINT",EDGE,{"derivedFrom":sQuery(id+"F8.wireOp",EDGE,"E15.4.0")}),1.0]])]});
            var Q109;
            Q109=makeQuery(id+"F8.imprint","IMPRINT",FACE,{"disambiguationData":[TD([[makeQuery(id+"F8.imprint","IMPRINT",EDGE,{"derivedFrom":sQuery(id+"F8.wireOp",EDGE,"E17.11.0")}),1.0]])]});
            var Q110;
            Q110=makeQuery(id+"F8.imprint","IMPRINT",FACE,{"disambiguationData":[TD([[makeQuery(id+"F8.imprint","IMPRINT",EDGE,{"derivedFrom":sQuery(id+"F8.wireOp",EDGE,"E17.12.0")}),1.0]])]});
            var Q111;
            Q111=makeQuery(id+"F8.imprint","IMPRINT",FACE,{"disambiguationData":[TD([[makeQuery(id+"F8.imprint","IMPRINT",EDGE,{"derivedFrom":sQuery(id+"F8.wireOp",EDGE,"E18.4.0")}),1.0]])]});
            var Q112;
            Q112=makeQuery(id+"F8.imprint","IMPRINT",FACE,{"disambiguationData":[TD([[makeQuery(id+"F8.imprint","IMPRINT",EDGE,{"derivedFrom":sQuery(id+"F8.wireOp",EDGE,"E19.5.0")}),1.0]])]});
            var Q113;
            Q113=makeQuery(id+"F8.imprint","IMPRINT",FACE,{"disambiguationData":[TD([[makeQuery(id+"F8.imprint","IMPRINT",EDGE,{"derivedFrom":sQuery(id+"F8.wireOp",EDGE,"E15.13.0")}),1.0]])]});
            var Q114;
            Q114=makeQuery(id+"F8.imprint","IMPRINT",FACE,{"disambiguationData":[TD([[makeQuery(id+"F8.imprint","IMPRINT",EDGE,{"derivedFrom":sQuery(id+"F8.wireOp",EDGE,"E19.9.0")}),1.0]])]});
            var Q115;
            Q115=makeQuery(id+"F8.imprint","IMPRINT",FACE,{"disambiguationData":[TD([[makeQuery(id+"F8.imprint","IMPRINT",EDGE,{"derivedFrom":sQuery(id+"F8.wireOp",EDGE,"E17.15.0")}),1.0]])]});
            var Q116;
            Q116=makeQuery(id+"F8.imprint","IMPRINT",FACE,{"disambiguationData":[TD([[makeQuery(id+"F8.imprint","IMPRINT",EDGE,{"derivedFrom":sQuery(id+"F8.wireOp",EDGE,"E18.8.0")}),1.0]])]});
            var Q117;
            Q117=makeQuery(id+"F8.imprint","IMPRINT",FACE,{"disambiguationData":[TD([[makeQuery(id+"F8.imprint","IMPRINT",EDGE,{"derivedFrom":sQuery(id+"F8.wireOp",EDGE,"E19.8.0")}),1.0]])]});
            var Q118;
            Q118=makeQuery(id+"F8.imprint","IMPRINT",FACE,{"disambiguationData":[TD([[makeQuery(id+"F8.imprint","IMPRINT",EDGE,{"derivedFrom":sQuery(id+"F8.wireOp",EDGE,"E18.18.0")}),1.0]])]});
            var Q119;
            Q119=makeQuery(id+"F8.imprint","IMPRINT",FACE,{"disambiguationData":[TD([[makeQuery(id+"F8.imprint","IMPRINT",EDGE,{"derivedFrom":sQuery(id+"F8.wireOp",EDGE,"E17.10.0")}),1.0]])]});
            var Q120;
            Q120=makeQuery(id+"F8.imprint","IMPRINT",FACE,{"disambiguationData":[TD([[makeQuery(id+"F8.imprint","IMPRINT",EDGE,{"derivedFrom":sQuery(id+"F8.wireOp",EDGE,"E17.17.0")}),1.0]])]});
            var Q121;
            Q121=makeQuery(id+"F8.imprint","IMPRINT",FACE,{"disambiguationData":[TD([[makeQuery(id+"F8.imprint","IMPRINT",EDGE,{"derivedFrom":sQuery(id+"F8.wireOp",EDGE,"E19.3.0")}),1.0]])]});
            extrude(context, id + "F9", {"entities" : qUnion([Q0, Q1, Q2, Q3, Q4, Q5, Q6, Q7, Q8, Q9, Q10, Q11, Q12, Q13, Q14, Q15, Q16, Q17, Q18, Q19, Q20, Q21, Q22, Q23, Q24, Q25, Q26, Q27, Q28, Q29, Q30, Q31, Q32, Q33, Q34, Q35, Q36, Q37, Q38, Q39, Q40, Q41, Q42, Q43, Q44, Q45, Q46, Q47, Q48, Q49, Q50, Q51, Q52, Q53, Q54, Q55, Q56, Q57, Q58, Q59, Q60, Q61, Q62, Q63, Q64, Q65, Q66, Q67, Q68, Q69, Q70, Q71, Q72, Q73, Q74, Q75, Q76, Q77, Q78, Q79, Q80, Q81, Q82, Q83, Q84, Q85, Q86, Q87, Q88, Q89, Q90, Q91, Q92, Q93, Q94, Q95, Q96, Q97, Q98, Q99, Q100, Q101, Q102, Q103, Q104, Q105, Q106, Q107, Q108, Q109, Q110, Q111, Q112, Q113, Q114, Q115, Q116, Q117, Q118, Q119, Q120, Q121]), "operationType" : NewBodyOperationType.REMOVE, "endBound" : BoundingType.THROUGH_ALL, "oppositeDirection" : true, "depth" : 25 * mm, "offsetDistance" : 25 * mm});
        }
        {
            var Q0;
            Q0=qCreatedBy(makeId("Front.planeOp"),FACE);
            var sketch = newSketch(context, id + "F10", { "sketchPlane" : qUnion([Q0])});
            skLineSegment(sketch, "E20", {"start": v(0, 0) * mm, "end": v(4, 0) * mm});
            skLineSegment(sketch, "E21", {"start": v(4, 0) * mm, "end": v(4, 20) * mm});
            skLineSegment(sketch, "E22", {"start": v(4, 20) * mm, "end": v(9, 20) * mm});
            skLineSegment(sketch, "E23", {"start": v(9, 20) * mm, "end": v(7.71, 22) * mm});
            skLineSegment(sketch, "E24", {"start": v(7.71, 22) * mm, "end": v(0, 22) * mm});
            skLineSegment(sketch, "E25", {"start": v(0, 22) * mm, "end": v(0, 0) * mm});
            skLineSegment(sketch, "E26", {"start": v(0, 30.8) * mm, "end": v(0, -5.78) * mm, "construction": true});
            skSolve(sketch);
        }
        {
            var Q0;
            Q0=makeQuery(id+"F10.imprint","IMPRINT",FACE,{"disambiguationData":[TD([[makeQuery(id+"F10.imprint","IMPRINT",EDGE,{"derivedFrom":sQuery(id+"F10.wireOp",EDGE,"E20")}),1.0]])]});
            var Q1;
            Q1=sQuery(id+"F10.wireOp",EDGE,"E26");
            revolve(context, id + "F11", {"operationType" : NewBodyOperationType.ADD, "surfaceOperationType" : NewSurfaceOperationType.NEW, "entities" : qUnion([Q0]), "axis" : qUnion([Q1]), "revolveType" : RevolveType.FULL});
        }
        {
            var Q0;
            Q0=makeQuery(id+"F6.opExtrude","CAP_EDGE",EDGE,{"disambiguationData":[OSD([sQuery(id+"F5.wireOp",EDGE,"E7.0")])],"isStart":true});
            chamfer(context, id + "F12", {"entities" : qUnion([Q0]), "chamferType" : ChamferType.OFFSET_ANGLE, "width" : 8 * mm, "oppositeDirection" : false, "angle" : 20 * degree, "tangentPropagation" : true});
        }
        {
            var Q0;
            Q0=qCreatedBy(makeId("Top.planeOp"),FACE);
            cPlane(context, id + "F13", {"entities" : qUnion([Q0]), "cplaneType" : CPlaneType.OFFSET, "offset" : 12.5 * mm, "width" : 150 * mm, "height" : 150 * mm});
        }
        {
            var Q0;
            Q0=qCreatedBy(id+"F13.planeOp",FACE);
            var sketch = newSketch(context, id + "F14", { "sketchPlane" : qUnion([Q0])});
            skLineSegment(sketch, "E27.bottom", {"start": v(2, 42.1) * mm, "end": v(-2, 42.1) * mm});
            skLineSegment(sketch, "E27.top", {"start": v(2, 35.44) * mm, "end": v(-2, 35.44) * mm});
            skLineSegment(sketch, "E27.left", {"start": v(2, 42.1) * mm, "end": v(2, 35.44) * mm});
            skLineSegment(sketch, "E27.right", {"start": v(-2, 42.1) * mm, "end": v(-2, 35.44) * mm});
            skPoint(sketch, "E27.middle", {"position": v(0, 38.77) * mm});
            skLineSegment(sketch, "E28.1.0", {"start": v(-8.53, 41.28) * mm, "end": v(-12.4, 40.29) * mm});
            skLineSegment(sketch, "E28.1.1", {"start": v(-12.4, 40.29) * mm, "end": v(-10.75, 33.83) * mm});
            skLineSegment(sketch, "E28.1.2", {"start": v(-6.88, 34.82) * mm, "end": v(-10.75, 33.83) * mm});
            skLineSegment(sketch, "E28.1.3", {"start": v(-8.53, 41.28) * mm, "end": v(-6.88, 34.82) * mm});
            skLineSegment(sketch, "E28.2.0", {"start": v(-18.53, 37.86) * mm, "end": v(-22.04, 35.94) * mm});
            skLineSegment(sketch, "E28.2.1", {"start": v(-22.04, 35.94) * mm, "end": v(-18.82, 30.1) * mm});
            skLineSegment(sketch, "E28.2.2", {"start": v(-15.32, 32.02) * mm, "end": v(-18.82, 30.1) * mm});
            skLineSegment(sketch, "E28.2.3", {"start": v(-18.53, 37.86) * mm, "end": v(-15.32, 32.02) * mm});
            skLineSegment(sketch, "E28.3.0", {"start": v(-27.37, 32.06) * mm, "end": v(-30.28, 29.33) * mm});
            skLineSegment(sketch, "E28.3.1", {"start": v(-30.28, 29.33) * mm, "end": v(-25.72, 24.46) * mm});
            skLineSegment(sketch, "E28.3.2", {"start": v(-22.8, 27.2) * mm, "end": v(-25.72, 24.46) * mm});
            skLineSegment(sketch, "E28.3.3", {"start": v(-27.37, 32.06) * mm, "end": v(-22.8, 27.2) * mm});
            skLineSegment(sketch, "E28.4.0", {"start": v(-34.48, 24.25) * mm, "end": v(-36.62, 20.87) * mm});
            skLineSegment(sketch, "E28.4.1", {"start": v(-36.62, 20.87) * mm, "end": v(-31, 17.3) * mm});
            skLineSegment(sketch, "E28.4.2", {"start": v(-28.85, 20.68) * mm, "end": v(-31, 17.3) * mm});
            skLineSegment(sketch, "E28.4.3", {"start": v(-34.48, 24.25) * mm, "end": v(-28.85, 20.68) * mm});
            skLineSegment(sketch, "E28.5.0", {"start": v(-39.43, 14.91) * mm, "end": v(-40.66, 11.1) * mm});
            skLineSegment(sketch, "E28.5.1", {"start": v(-40.66, 11.1) * mm, "end": v(-34.32, 9.05) * mm});
            skLineSegment(sketch, "E28.5.2", {"start": v(-33.08, 12.85) * mm, "end": v(-34.32, 9.05) * mm});
            skLineSegment(sketch, "E28.5.3", {"start": v(-39.43, 14.91) * mm, "end": v(-33.08, 12.85) * mm});
            skLineSegment(sketch, "E28.6.0", {"start": v(-41.9, 4.64) * mm, "end": v(-42.15, 0.65) * mm});
            skLineSegment(sketch, "E28.6.1", {"start": v(-42.15, 0.65) * mm, "end": v(-35.5, 0.23) * mm});
            skLineSegment(sketch, "E28.6.2", {"start": v(-35.24, 4.22) * mm, "end": v(-35.5, 0.23) * mm});
            skLineSegment(sketch, "E28.6.3", {"start": v(-41.9, 4.64) * mm, "end": v(-35.24, 4.22) * mm});
            skLineSegment(sketch, "E28.7.0", {"start": v(-41.74, -5.93) * mm, "end": v(-40.99, -9.85) * mm});
            skLineSegment(sketch, "E28.7.1", {"start": v(-40.99, -9.85) * mm, "end": v(-34.43, -8.6) * mm});
            skLineSegment(sketch, "E28.7.2", {"start": v(-35.18, -4.68) * mm, "end": v(-34.43, -8.6) * mm});
            skLineSegment(sketch, "E28.7.3", {"start": v(-41.74, -5.93) * mm, "end": v(-35.18, -4.68) * mm});
            skLineSegment(sketch, "E28.8.0", {"start": v(-38.95, -16.12) * mm, "end": v(-37.25, -19.74) * mm});
            skLineSegment(sketch, "E28.8.1", {"start": v(-37.25, -19.74) * mm, "end": v(-31.21, -16.9) * mm});
            skLineSegment(sketch, "E28.8.2", {"start": v(-32.92, -13.28) * mm, "end": v(-31.21, -16.9) * mm});
            skLineSegment(sketch, "E28.8.3", {"start": v(-38.95, -16.12) * mm, "end": v(-32.92, -13.28) * mm});
            skLineSegment(sketch, "E28.9.0", {"start": v(-33.72, -25.3) * mm, "end": v(-31.17, -28.38) * mm});
            skLineSegment(sketch, "E28.9.1", {"start": v(-31.17, -28.38) * mm, "end": v(-26.03, -24.13) * mm});
            skLineSegment(sketch, "E28.9.2", {"start": v(-28.58, -21.05) * mm, "end": v(-26.03, -24.13) * mm});
            skLineSegment(sketch, "E28.9.3", {"start": v(-33.72, -25.3) * mm, "end": v(-28.58, -21.05) * mm});
            skLineSegment(sketch, "E28.10.0", {"start": v(-26.37, -32.89) * mm, "end": v(-23.13, -35.24) * mm});
            skLineSegment(sketch, "E28.10.1", {"start": v(-23.13, -35.24) * mm, "end": v(-19.21, -29.84) * mm});
            skLineSegment(sketch, "E28.10.2", {"start": v(-22.45, -27.5) * mm, "end": v(-19.21, -29.84) * mm});
            skLineSegment(sketch, "E28.10.3", {"start": v(-26.37, -32.89) * mm, "end": v(-22.45, -27.5) * mm});
            skLineSegment(sketch, "E28.11.0", {"start": v(-17.36, -38.41) * mm, "end": v(-13.64, -39.89) * mm});
            skLineSegment(sketch, "E28.11.1", {"start": v(-13.64, -39.89) * mm, "end": v(-11.19, -33.68) * mm});
            skLineSegment(sketch, "E28.11.2", {"start": v(-14.9, -32.21) * mm, "end": v(-11.19, -33.68) * mm});
            skLineSegment(sketch, "E28.11.3", {"start": v(-17.36, -38.41) * mm, "end": v(-14.9, -32.21) * mm});
            skLineSegment(sketch, "E28.12.0", {"start": v(-7.26, -41.52) * mm, "end": v(-3.3, -42.03) * mm});
            skLineSegment(sketch, "E28.12.1", {"start": v(-3.3, -42.03) * mm, "end": v(-2.46, -35.4) * mm});
            skLineSegment(sketch, "E28.12.2", {"start": v(-6.43, -34.9) * mm, "end": v(-2.46, -35.4) * mm});
            skLineSegment(sketch, "E28.12.3", {"start": v(-7.26, -41.52) * mm, "end": v(-6.43, -34.9) * mm});
            skLineSegment(sketch, "E28.13.0", {"start": v(3.3, -42.03) * mm, "end": v(7.26, -41.52) * mm});
            skLineSegment(sketch, "E28.13.1", {"start": v(7.26, -41.52) * mm, "end": v(6.43, -34.9) * mm});
            skLineSegment(sketch, "E28.13.2", {"start": v(2.46, -35.4) * mm, "end": v(6.43, -34.9) * mm});
            skLineSegment(sketch, "E28.13.3", {"start": v(3.3, -42.03) * mm, "end": v(2.46, -35.4) * mm});
            skLineSegment(sketch, "E28.14.0", {"start": v(13.64, -39.89) * mm, "end": v(17.36, -38.41) * mm});
            skLineSegment(sketch, "E28.14.1", {"start": v(17.36, -38.41) * mm, "end": v(14.9, -32.21) * mm});
            skLineSegment(sketch, "E28.14.2", {"start": v(11.19, -33.68) * mm, "end": v(14.9, -32.21) * mm});
            skLineSegment(sketch, "E28.14.3", {"start": v(13.64, -39.89) * mm, "end": v(11.19, -33.68) * mm});
            skLineSegment(sketch, "E28.15.0", {"start": v(23.13, -35.24) * mm, "end": v(26.37, -32.89) * mm});
            skLineSegment(sketch, "E28.15.1", {"start": v(26.37, -32.89) * mm, "end": v(22.45, -27.5) * mm});
            skLineSegment(sketch, "E28.15.2", {"start": v(19.21, -29.84) * mm, "end": v(22.45, -27.5) * mm});
            skLineSegment(sketch, "E28.15.3", {"start": v(23.13, -35.24) * mm, "end": v(19.21, -29.84) * mm});
            skLineSegment(sketch, "E28.16.0", {"start": v(31.17, -28.38) * mm, "end": v(33.72, -25.3) * mm});
            skLineSegment(sketch, "E28.16.1", {"start": v(33.72, -25.3) * mm, "end": v(28.58, -21.05) * mm});
            skLineSegment(sketch, "E28.16.2", {"start": v(26.03, -24.13) * mm, "end": v(28.58, -21.05) * mm});
            skLineSegment(sketch, "E28.16.3", {"start": v(31.17, -28.38) * mm, "end": v(26.03, -24.13) * mm});
            skLineSegment(sketch, "E28.17.0", {"start": v(37.25, -19.74) * mm, "end": v(38.95, -16.12) * mm});
            skLineSegment(sketch, "E28.17.1", {"start": v(38.95, -16.12) * mm, "end": v(32.92, -13.28) * mm});
            skLineSegment(sketch, "E28.17.2", {"start": v(31.21, -16.9) * mm, "end": v(32.92, -13.28) * mm});
            skLineSegment(sketch, "E28.17.3", {"start": v(37.25, -19.74) * mm, "end": v(31.21, -16.9) * mm});
            skLineSegment(sketch, "E28.18.0", {"start": v(40.99, -9.85) * mm, "end": v(41.74, -5.93) * mm});
            skLineSegment(sketch, "E28.18.1", {"start": v(41.74, -5.93) * mm, "end": v(35.18, -4.68) * mm});
            skLineSegment(sketch, "E28.18.2", {"start": v(34.43, -8.6) * mm, "end": v(35.18, -4.68) * mm});
            skLineSegment(sketch, "E28.18.3", {"start": v(40.99, -9.85) * mm, "end": v(34.43, -8.6) * mm});
            skLineSegment(sketch, "E28.19.0", {"start": v(42.15, 0.65) * mm, "end": v(41.9, 4.64) * mm});
            skLineSegment(sketch, "E28.19.1", {"start": v(41.9, 4.64) * mm, "end": v(35.24, 4.22) * mm});
            skLineSegment(sketch, "E28.19.2", {"start": v(35.5, 0.23) * mm, "end": v(35.24, 4.22) * mm});
            skLineSegment(sketch, "E28.19.3", {"start": v(42.15, 0.65) * mm, "end": v(35.5, 0.23) * mm});
            skLineSegment(sketch, "E28.20.0", {"start": v(40.66, 11.1) * mm, "end": v(39.43, 14.91) * mm});
            skLineSegment(sketch, "E28.20.1", {"start": v(39.43, 14.91) * mm, "end": v(33.08, 12.85) * mm});
            skLineSegment(sketch, "E28.20.2", {"start": v(34.32, 9.05) * mm, "end": v(33.08, 12.85) * mm});
            skLineSegment(sketch, "E28.20.3", {"start": v(40.66, 11.1) * mm, "end": v(34.32, 9.05) * mm});
            skLineSegment(sketch, "E28.21.0", {"start": v(36.62, 20.87) * mm, "end": v(34.48, 24.25) * mm});
            skLineSegment(sketch, "E28.21.1", {"start": v(34.48, 24.25) * mm, "end": v(28.85, 20.68) * mm});
            skLineSegment(sketch, "E28.21.2", {"start": v(31, 17.3) * mm, "end": v(28.85, 20.68) * mm});
            skLineSegment(sketch, "E28.21.3", {"start": v(36.62, 20.87) * mm, "end": v(31, 17.3) * mm});
            skLineSegment(sketch, "E28.22.0", {"start": v(30.28, 29.33) * mm, "end": v(27.37, 32.06) * mm});
            skLineSegment(sketch, "E28.22.1", {"start": v(27.37, 32.06) * mm, "end": v(22.8, 27.2) * mm});
            skLineSegment(sketch, "E28.22.2", {"start": v(25.72, 24.46) * mm, "end": v(22.8, 27.2) * mm});
            skLineSegment(sketch, "E28.22.3", {"start": v(30.28, 29.33) * mm, "end": v(25.72, 24.46) * mm});
            skLineSegment(sketch, "E28.23.0", {"start": v(22.04, 35.94) * mm, "end": v(18.53, 37.86) * mm});
            skLineSegment(sketch, "E28.23.1", {"start": v(18.53, 37.86) * mm, "end": v(15.32, 32.02) * mm});
            skLineSegment(sketch, "E28.23.2", {"start": v(18.82, 30.1) * mm, "end": v(15.32, 32.02) * mm});
            skLineSegment(sketch, "E28.23.3", {"start": v(22.04, 35.94) * mm, "end": v(18.82, 30.1) * mm});
            skLineSegment(sketch, "E28.24.0", {"start": v(12.4, 40.29) * mm, "end": v(8.53, 41.28) * mm});
            skLineSegment(sketch, "E28.24.1", {"start": v(8.53, 41.28) * mm, "end": v(6.88, 34.82) * mm});
            skLineSegment(sketch, "E28.24.2", {"start": v(10.75, 33.83) * mm, "end": v(6.88, 34.82) * mm});
            skLineSegment(sketch, "E28.24.3", {"start": v(12.4, 40.29) * mm, "end": v(10.75, 33.83) * mm});
            skPoint(sketch, "E28.center", {"position": v(0, 0) * mm});
            skSolve(sketch);
        }
        {
            var Q0;
            Q0=makeQuery(id+"F14.imprint","IMPRINT",FACE,{"disambiguationData":[TD([[makeQuery(id+"F14.imprint","IMPRINT",EDGE,{"derivedFrom":sQuery(id+"F14.wireOp",EDGE,"E28.12.0")}),1.0]])]});
            var Q1;
            Q1=makeQuery(id+"F14.imprint","IMPRINT",FACE,{"disambiguationData":[TD([[makeQuery(id+"F14.imprint","IMPRINT",EDGE,{"derivedFrom":sQuery(id+"F14.wireOp",EDGE,"E27.bottom")}),1.0]])]});
            var Q2;
            Q2=makeQuery(id+"F14.imprint","IMPRINT",FACE,{"disambiguationData":[TD([[makeQuery(id+"F14.imprint","IMPRINT",EDGE,{"derivedFrom":sQuery(id+"F14.wireOp",EDGE,"E28.2.0")}),1.0]])]});
            var Q3;
            Q3=makeQuery(id+"F14.imprint","IMPRINT",FACE,{"disambiguationData":[TD([[makeQuery(id+"F14.imprint","IMPRINT",EDGE,{"derivedFrom":sQuery(id+"F14.wireOp",EDGE,"E28.14.0")}),1.0]])]});
            var Q4;
            Q4=makeQuery(id+"F14.imprint","IMPRINT",FACE,{"disambiguationData":[TD([[makeQuery(id+"F14.imprint","IMPRINT",EDGE,{"derivedFrom":sQuery(id+"F14.wireOp",EDGE,"E28.3.0")}),1.0]])]});
            var Q5;
            Q5=makeQuery(id+"F14.imprint","IMPRINT",FACE,{"disambiguationData":[TD([[makeQuery(id+"F14.imprint","IMPRINT",EDGE,{"derivedFrom":sQuery(id+"F14.wireOp",EDGE,"E28.15.0")}),1.0]])]});
            var Q6;
            Q6=makeQuery(id+"F14.imprint","IMPRINT",FACE,{"disambiguationData":[TD([[makeQuery(id+"F14.imprint","IMPRINT",EDGE,{"derivedFrom":sQuery(id+"F14.wireOp",EDGE,"E28.16.0")}),1.0]])]});
            var Q7;
            Q7=makeQuery(id+"F14.imprint","IMPRINT",FACE,{"disambiguationData":[TD([[makeQuery(id+"F14.imprint","IMPRINT",EDGE,{"derivedFrom":sQuery(id+"F14.wireOp",EDGE,"E28.23.0")}),1.0]])]});
            var Q8;
            Q8=makeQuery(id+"F14.imprint","IMPRINT",FACE,{"disambiguationData":[TD([[makeQuery(id+"F14.imprint","IMPRINT",EDGE,{"derivedFrom":sQuery(id+"F14.wireOp",EDGE,"E28.13.0")}),1.0]])]});
            var Q9;
            Q9=makeQuery(id+"F14.imprint","IMPRINT",FACE,{"disambiguationData":[TD([[makeQuery(id+"F14.imprint","IMPRINT",EDGE,{"derivedFrom":sQuery(id+"F14.wireOp",EDGE,"E28.21.0")}),1.0]])]});
            var Q10;
            Q10=makeQuery(id+"F14.imprint","IMPRINT",FACE,{"disambiguationData":[TD([[makeQuery(id+"F14.imprint","IMPRINT",EDGE,{"derivedFrom":sQuery(id+"F14.wireOp",EDGE,"E28.4.0")}),1.0]])]});
            var Q11;
            Q11=makeQuery(id+"F14.imprint","IMPRINT",FACE,{"disambiguationData":[TD([[makeQuery(id+"F14.imprint","IMPRINT",EDGE,{"derivedFrom":sQuery(id+"F14.wireOp",EDGE,"E28.6.0")}),1.0]])]});
            var Q12;
            Q12=makeQuery(id+"F14.imprint","IMPRINT",FACE,{"disambiguationData":[TD([[makeQuery(id+"F14.imprint","IMPRINT",EDGE,{"derivedFrom":sQuery(id+"F14.wireOp",EDGE,"E28.24.0")}),1.0]])]});
            var Q13;
            Q13=makeQuery(id+"F14.imprint","IMPRINT",FACE,{"disambiguationData":[TD([[makeQuery(id+"F14.imprint","IMPRINT",EDGE,{"derivedFrom":sQuery(id+"F14.wireOp",EDGE,"E28.10.0")}),1.0]])]});
            var Q14;
            Q14=makeQuery(id+"F14.imprint","IMPRINT",FACE,{"disambiguationData":[TD([[makeQuery(id+"F14.imprint","IMPRINT",EDGE,{"derivedFrom":sQuery(id+"F14.wireOp",EDGE,"E28.11.0")}),1.0]])]});
            var Q15;
            Q15=makeQuery(id+"F14.imprint","IMPRINT",FACE,{"disambiguationData":[TD([[makeQuery(id+"F14.imprint","IMPRINT",EDGE,{"derivedFrom":sQuery(id+"F14.wireOp",EDGE,"E28.1.0")}),1.0]])]});
            var Q16;
            Q16=makeQuery(id+"F14.imprint","IMPRINT",FACE,{"disambiguationData":[TD([[makeQuery(id+"F14.imprint","IMPRINT",EDGE,{"derivedFrom":sQuery(id+"F14.wireOp",EDGE,"E28.5.0")}),1.0]])]});
            var Q17;
            Q17=makeQuery(id+"F14.imprint","IMPRINT",FACE,{"disambiguationData":[TD([[makeQuery(id+"F14.imprint","IMPRINT",EDGE,{"derivedFrom":sQuery(id+"F14.wireOp",EDGE,"E28.22.0")}),1.0]])]});
            var Q18;
            Q18=makeQuery(id+"F14.imprint","IMPRINT",FACE,{"disambiguationData":[TD([[makeQuery(id+"F14.imprint","IMPRINT",EDGE,{"derivedFrom":sQuery(id+"F14.wireOp",EDGE,"E28.19.0")}),1.0]])]});
            var Q19;
            Q19=makeQuery(id+"F14.imprint","IMPRINT",FACE,{"disambiguationData":[TD([[makeQuery(id+"F14.imprint","IMPRINT",EDGE,{"derivedFrom":sQuery(id+"F14.wireOp",EDGE,"E28.8.0")}),1.0]])]});
            var Q20;
            Q20=makeQuery(id+"F14.imprint","IMPRINT",FACE,{"disambiguationData":[TD([[makeQuery(id+"F14.imprint","IMPRINT",EDGE,{"derivedFrom":sQuery(id+"F14.wireOp",EDGE,"E28.7.0")}),1.0]])]});
            var Q21;
            Q21=makeQuery(id+"F14.imprint","IMPRINT",FACE,{"disambiguationData":[TD([[makeQuery(id+"F14.imprint","IMPRINT",EDGE,{"derivedFrom":sQuery(id+"F14.wireOp",EDGE,"E28.9.0")}),1.0]])]});
            var Q22;
            Q22=makeQuery(id+"F14.imprint","IMPRINT",FACE,{"disambiguationData":[TD([[makeQuery(id+"F14.imprint","IMPRINT",EDGE,{"derivedFrom":sQuery(id+"F14.wireOp",EDGE,"E28.20.0")}),1.0]])]});
            var Q23;
            Q23=makeQuery(id+"F14.imprint","IMPRINT",FACE,{"disambiguationData":[TD([[makeQuery(id+"F14.imprint","IMPRINT",EDGE,{"derivedFrom":sQuery(id+"F14.wireOp",EDGE,"E28.18.0")}),1.0]])]});
            var Q24;
            Q24=makeQuery(id+"F14.imprint","IMPRINT",FACE,{"disambiguationData":[TD([[makeQuery(id+"F14.imprint","IMPRINT",EDGE,{"derivedFrom":sQuery(id+"F14.wireOp",EDGE,"E28.17.0")}),1.0]])]});
            extrude(context, id + "F15", {"entities" : qUnion([Q0, Q1, Q2, Q3, Q4, Q5, Q6, Q7, Q8, Q9, Q10, Q11, Q12, Q13, Q14, Q15, Q16, Q17, Q18, Q19, Q20, Q21, Q22, Q23, Q24]), "operationType" : NewBodyOperationType.REMOVE, "endBound" : BoundingType.SYMMETRIC, "oppositeDirection" : true, "depth" : 14 * mm, "offsetDistance" : 25 * mm});
        }
    });
